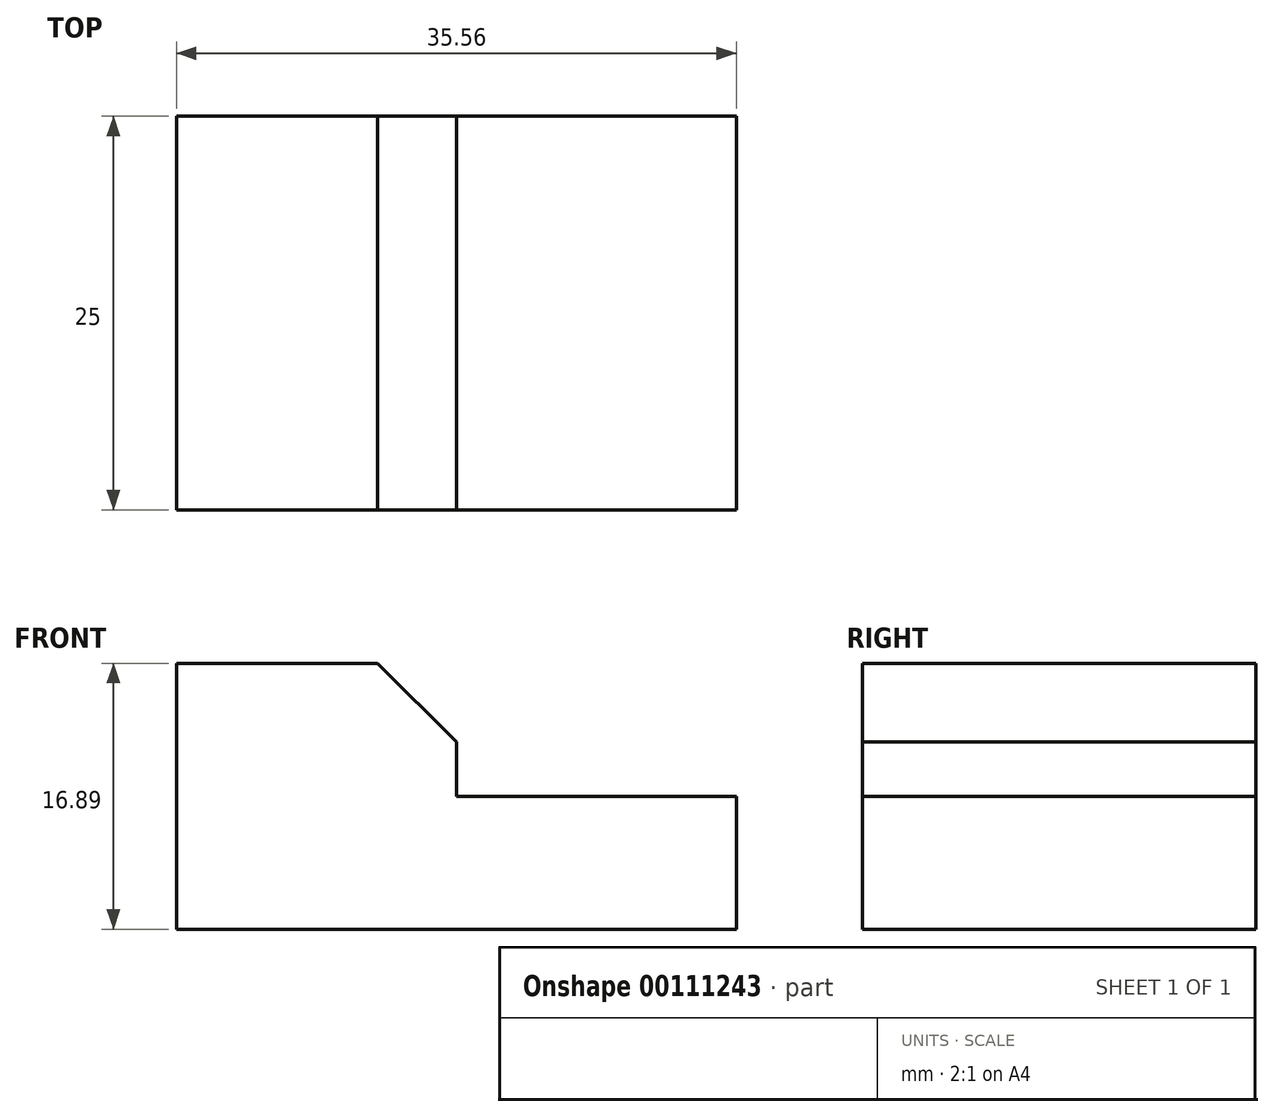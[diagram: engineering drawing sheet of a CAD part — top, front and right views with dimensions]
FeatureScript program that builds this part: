
annotation { "Feature Type Name" : "Feature", "Feature Type Description" : "" }
export const myFeature = defineFeature(function(context is Context, id is Id, definition is map)
    precondition{}
    {
        {
            var Q0;
            Q0=qCreatedBy(makeId("Front.planeOp"),FACE);
            var sketch = newSketch(context, id + "F0", { "sketchPlane" : qUnion([Q0])});
            skLineSegment(sketch, "E0.bottom", {"start": v(-10.9, 8.89) * mm, "end": v(-46.45, 8.89) * mm});
            skLineSegment(sketch, "E0.top", {"start": v(-28.67, 25.78) * mm, "end": v(-46.45, 25.78) * mm});
            skLineSegment(sketch, "E0.left", {"start": v(-10.9, 8.89) * mm, "end": v(-10.9, 17.33) * mm});
            skLineSegment(sketch, "E0.right", {"start": v(-46.45, 8.89) * mm, "end": v(-46.45, 25.78) * mm});
            skPoint(sketch, "E0.middle", {"position": v(-28.67, 17.33) * mm});
            skLineSegment(sketch, "E1", {"start": v(-28.67, 17.33) * mm, "end": v(-10.9, 17.33) * mm});
            skLineSegment(sketch, "E2", {"start": v(-28.67, 17.33) * mm, "end": v(-28.67, 25.78) * mm});
            skSolve(sketch);
        }
        {
            var Q0;
            Q0=makeQuery(id+"F0.imprint","IMPRINT",FACE,{"disambiguationData":[TD([[makeQuery(id+"F0.imprint","IMPRINT",EDGE,{"derivedFrom":sQuery(id+"F0.wireOp",EDGE,"E0.bottom")}),-1.0]])]});
            extrude(context, id + "F1", {"entities" : qUnion([Q0]), "endBound" : BoundingType.SYMMETRIC, "depth" : 25 * mm});
        }
        {
            var Q0;
            Q0=makeQuery(id+"F1.opExtrude","SWEPT_EDGE",EDGE,{"disambiguationData":[OSD([sQuery(id+"F0.wireOp",EDGE,"E0.top"),sQuery(id+"F0.wireOp",EDGE,"E2")])]});
            chamfer(context, id + "F2", {"entities" : qUnion([Q0]), "width" : 5 * mm, "tangentPropagation" : true});
        }
    });
